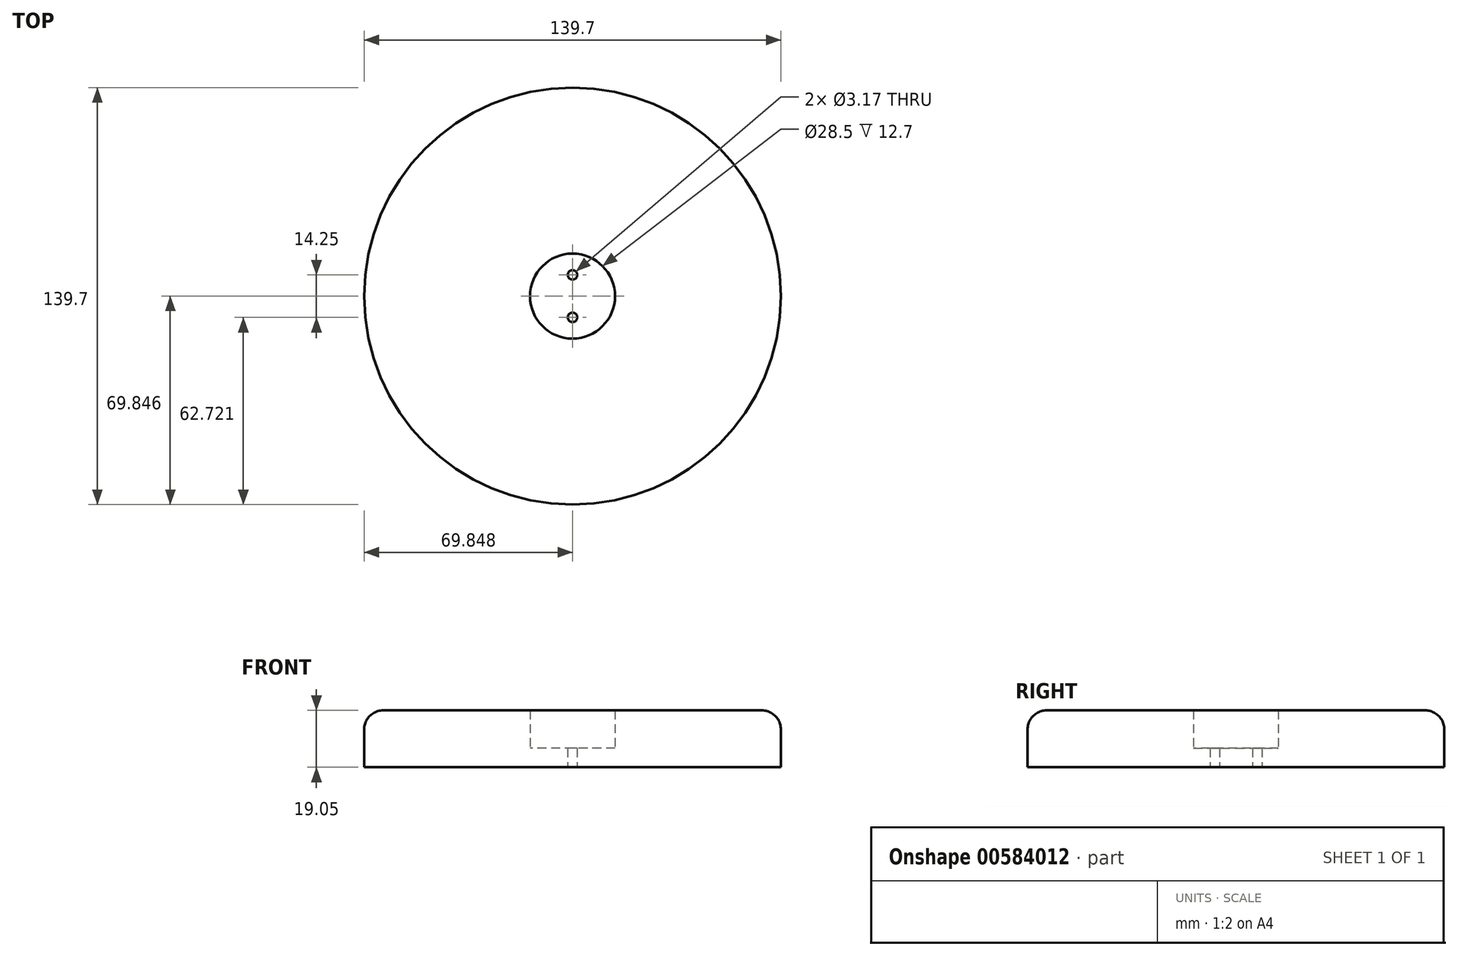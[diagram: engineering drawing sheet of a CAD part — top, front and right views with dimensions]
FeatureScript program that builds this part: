
annotation { "Feature Type Name" : "Feature", "Feature Type Description" : "" }
export const myFeature = defineFeature(function(context is Context, id is Id, definition is map)
    precondition{}
    {
        {
            var Q0;
            Q0=qCreatedBy(makeId("Top.planeOp"),FACE);
            var sketch = newSketch(context, id + "F0", { "sketchPlane" : qUnion([Q0])});
            skCircle(sketch, "E0", {"center": v(91.95, 93.34) * mm, "radius": 69.85 * mm});
            skCircle(sketch, "E1", {"center": v(91.95, 93.34) * mm, "radius": 14.25 * mm});
            skCircle(sketch, "E2", {"center": v(91.95, 86.21) * mm, "radius": 1.59 * mm});
            skCircle(sketch, "E3", {"center": v(91.95, 100.46) * mm, "radius": 1.59 * mm});
            skSolve(sketch);
        }
        {
            var Q0;
            Q0=makeQuery(id+"F0.imprint","IMPRINT",FACE,{"disambiguationData":[TD([[makeQuery(id+"F0.imprint","IMPRINT",EDGE,{"derivedFrom":sQuery(id+"F0.wireOp",EDGE,"E0")}),1.0]])]});
            extrude(context, id + "F1", {"entities" : qUnion([Q0]), "depth" : 19.05 * mm, "offsetDistance" : 25.4 * mm});
        }
        {
            var Q0;
            Q0=makeQuery(id+"F0.imprint","IMPRINT",FACE,{"disambiguationData":[TD([[makeQuery(id+"F0.imprint","IMPRINT",EDGE,{"derivedFrom":sQuery(id+"F0.wireOp",EDGE,"E1")}),1.0]])]});
            extrude(context, id + "F2", {"entities" : qUnion([Q0]), "operationType" : NewBodyOperationType.ADD, "depth" : 6.35 * mm, "offsetDistance" : 25.4 * mm});
        }
        {
            var Q0;
            Q0=makeQuery(id+"F1.opExtrude","CAP_EDGE",EDGE,{"disambiguationData":[OSD([sQuery(id+"F0.wireOp",EDGE,"E0")])],"isStart":false});
            fillet(context, id + "F3", {"entities" : qUnion([Q0]), "radius" : 6.35 * mm, "tangentPropagation" : true, "allowEdgeOverflow" : false});
        }
    });
